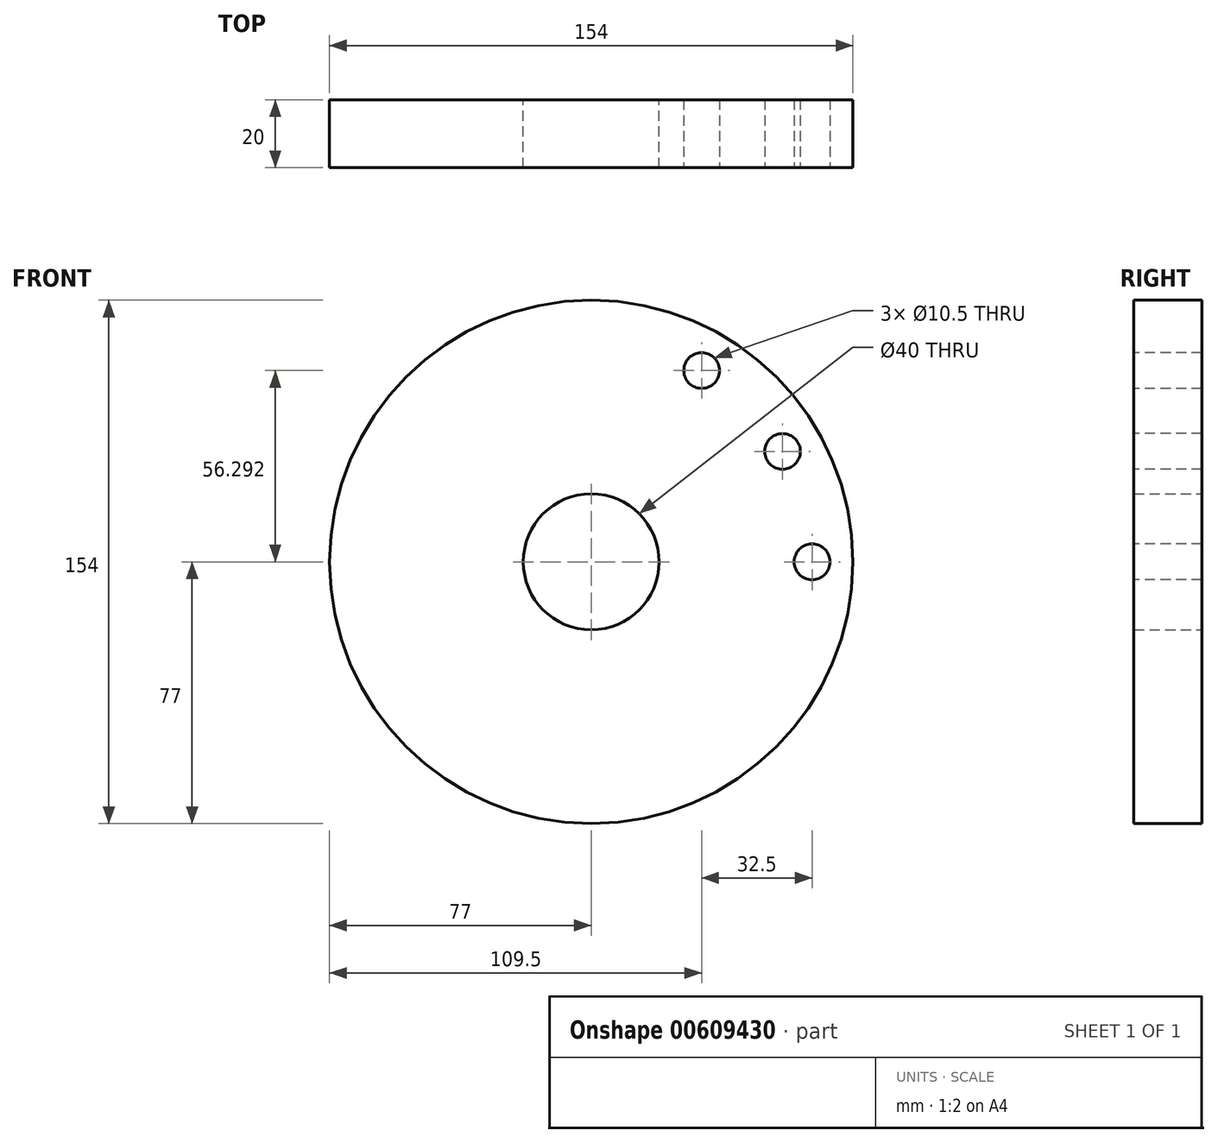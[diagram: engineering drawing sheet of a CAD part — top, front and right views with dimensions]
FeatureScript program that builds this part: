
annotation { "Feature Type Name" : "Feature", "Feature Type Description" : "" }
export const myFeature = defineFeature(function(context is Context, id is Id, definition is map)
    precondition{}
    {
        {
            var Q0;
            Q0=qCreatedBy(makeId("Front.planeOp"),FACE);
            var sketch = newSketch(context, id + "F0", { "sketchPlane" : qUnion([Q0])});
            skCircle(sketch, "E0", {"center": v(0, 0) * mm, "radius": 77 * mm});
            skCircle(sketch, "E1", {"center": v(0, 0) * mm, "radius": 20 * mm});
            skSolve(sketch);
        }
        {
            var Q0;
            Q0=makeQuery(id+"F0.imprint","IMPRINT",FACE,{"disambiguationData":[TD([[makeQuery(id+"F0.imprint","IMPRINT",EDGE,{"derivedFrom":sQuery(id+"F0.wireOp",EDGE,"E0")}),1.0]])]});
            extrude(context, id + "F1", {"entities" : qUnion([Q0]), "depth" : 20 * mm, "offsetDistance" : 25 * mm});
        }
        {
            var Q0;
            Q0=makeQuery(id+"F1.opExtrude","CAP_FACE",FACE,{"disambiguationData":[OSD([sQuery(id+"F0.wireOp",EDGE,"E0"),sQuery(id+"F0.wireOp",EDGE,"E1")])],"isStart":false});
            var sketch = newSketch(context, id + "F2", { "sketchPlane" : qUnion([Q0])});
            skCircle(sketch, "E2", {"center": v(0, 0) * mm, "radius": 65 * mm});
            skCircle(sketch, "E3", {"center": v(65, 0) * mm, "radius": 5.25 * mm});
            skCircle(sketch, "E4.1.0", {"center": v(56.3, 32.5) * mm, "radius": 5.25 * mm});
            skCircle(sketch, "E4.2.0", {"center": v(32.5, 56.3) * mm, "radius": 5.25 * mm});
            skCircle(sketch, "E4.3.0", {"center": v(0, 65) * mm, "radius": 5.25 * mm});
            skCircle(sketch, "E4.4.0", {"center": v(-32.5, 56.3) * mm, "radius": 5.25 * mm});
            skCircle(sketch, "E4.5.0", {"center": v(-56.3, 32.5) * mm, "radius": 5.25 * mm});
            skCircle(sketch, "E4.6.0", {"center": v(-65, 0) * mm, "radius": 5.25 * mm});
            skCircle(sketch, "E4.7.0", {"center": v(-56.3, -32.5) * mm, "radius": 5.25 * mm});
            skCircle(sketch, "E4.8.0", {"center": v(-32.5, -56.3) * mm, "radius": 5.25 * mm});
            skCircle(sketch, "E4.9.0", {"center": v(0, -65) * mm, "radius": 5.25 * mm});
            skCircle(sketch, "E4.10.0", {"center": v(32.5, -56.3) * mm, "radius": 5.25 * mm});
            skCircle(sketch, "E4.11.0", {"center": v(56.3, -32.5) * mm, "radius": 5.25 * mm});
            skSolve(sketch);
        }
        {
            var Q0;
            Q0=sQuery(id+"F2.wireOp",VERTEX,"E4.11.0.center");
            var Q1;
            Q1=sQuery(id+"F2.wireOp",VERTEX,"E3.center");
            var Q2;
            Q2=sQuery(id+"F2.wireOp",VERTEX,"E4.1.0.center");
            var Q3;
            Q3=sQuery(id+"F2.wireOp",VERTEX,"E4.2.0.center");
            var Q4;
            Q4=sQuery(id+"F2.wireOp",VERTEX,"E4.3.0.center");
            var Q5;
            Q5=sQuery(id+"F2.wireOp",VERTEX,"E4.4.0.center");
            var Q6;
            Q6=sQuery(id+"F2.wireOp",VERTEX,"E4.5.0.center");
            var Q7;
            Q7=sQuery(id+"F2.wireOp",VERTEX,"E4.6.0.center");
            var Q8;
            Q8=sQuery(id+"F2.wireOp",VERTEX,"E4.7.0.center");
            var Q9;
            Q9=sQuery(id+"F2.wireOp",VERTEX,"E4.8.0.center");
            var Q10;
            Q10=sQuery(id+"F2.wireOp",VERTEX,"E4.9.0.center");
            var Q11;
            Q11=sQuery(id+"F2.wireOp",VERTEX,"E4.10.0.center");
            var Q12;
            Q12=makeQuery(id+"F1.opExtrude","SWEPT_BODY",BODY,{"disambiguationData":[OSD([sQuery(id+"F0.wireOp",EDGE,"E0"),sQuery(id+"F0.wireOp",EDGE,"E1")])]});
            hole(context, id + "F3", {"style" : HoleStyle.SIMPLE, "endStyle" : HoleEndStyle.THROUGH, "holeDiameter" : 10.5 * mm, "majorDiameter" : 5 * mm, "isTappedThrough" : true, "tappedDepth" : 12 * mm, "tapClearance" : 3, "locations" : qUnion([Q0, Q1, Q2, Q3, Q4, Q5, Q6, Q7, Q8, Q9, Q10, Q11]), "scope" : qUnion([Q12])});
        }
    });
